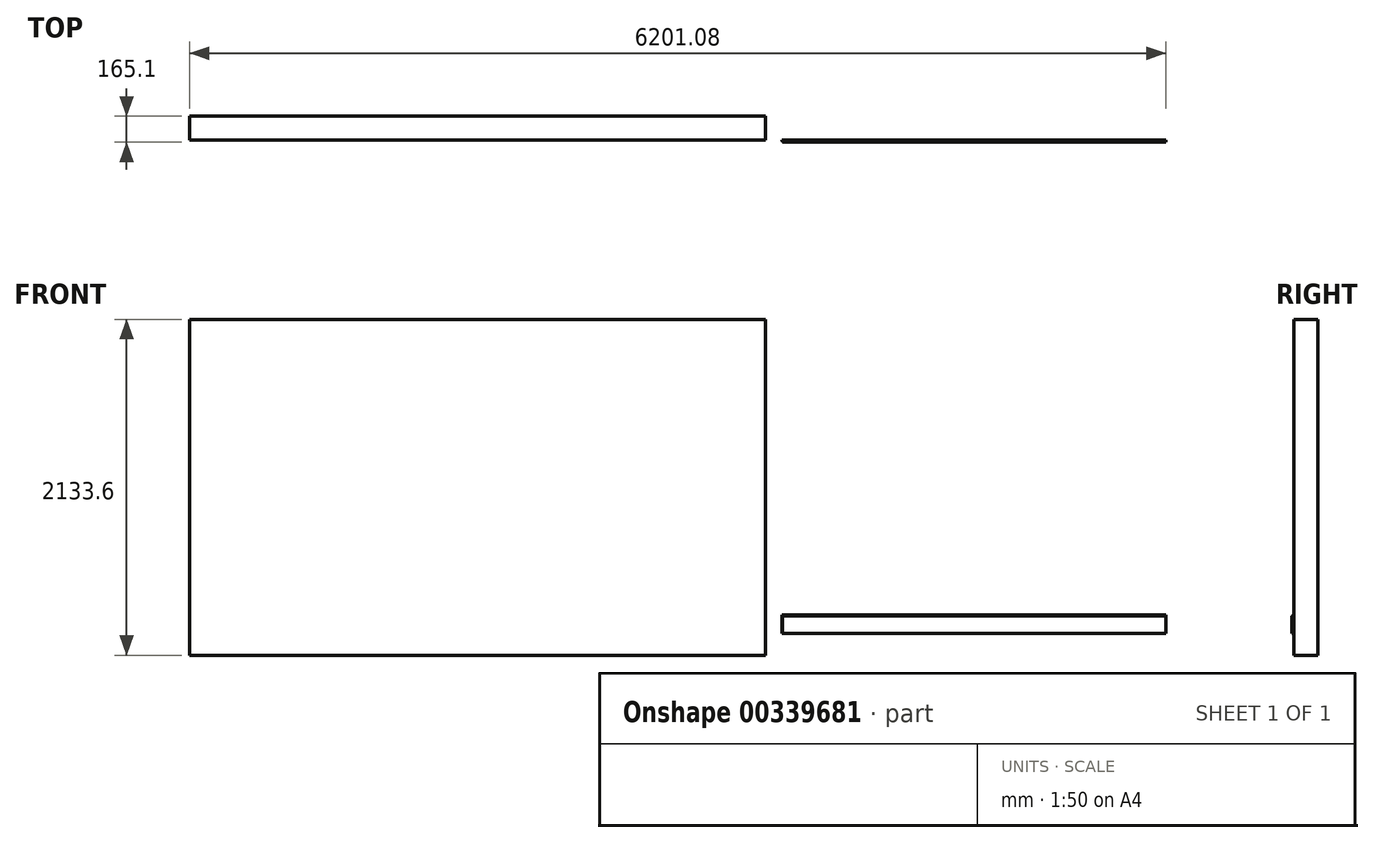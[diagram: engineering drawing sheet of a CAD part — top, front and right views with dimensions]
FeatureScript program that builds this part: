
annotation { "Feature Type Name" : "Feature", "Feature Type Description" : "" }
export const myFeature = defineFeature(function(context is Context, id is Id, definition is map)
    precondition{}
    {
        {
            var Q0;
            Q0=qCreatedBy(makeId("Front.planeOp"),FACE);
            var sketch = newSketch(context, id + "F0", { "sketchPlane" : qUnion([Q0])});
            skLineSegment(sketch, "E0.bottom", {"start": v(-3602.13, 2084.47) * mm, "end": v(55.47, 2084.47) * mm});
            skLineSegment(sketch, "E0.top", {"start": v(-3602.13, -49.13) * mm, "end": v(55.47, -49.13) * mm});
            skLineSegment(sketch, "E0.left", {"start": v(-3602.13, 2084.47) * mm, "end": v(-3602.13, -49.13) * mm});
            skLineSegment(sketch, "E0.right", {"start": v(55.47, 2084.47) * mm, "end": v(55.47, -49.13) * mm});
            skLineSegment(sketch, "E1.top", {"start": v(-3602.13, 90.57) * mm, "end": v(55.47, 90.57) * mm});
            skLineSegment(sketch, "E1.left", {"start": v(-3602.13, -49.13) * mm, "end": v(-3602.13, 90.57) * mm});
            skLineSegment(sketch, "E1.right", {"start": v(55.47, -49.13) * mm, "end": v(55.47, 90.57) * mm});
            skLineSegment(sketch, "E2.bottom", {"start": v(-736.02, 90.57) * mm, "end": v(160.55, 90.57) * mm});
            skLineSegment(sketch, "E2.top", {"start": v(-736.02, 208.05) * mm, "end": v(160.55, 208.05) * mm});
            skLineSegment(sketch, "E2.left", {"start": v(160.55, 90.57) * mm, "end": v(160.55, 208.05) * mm});
            skLineSegment(sketch, "E2.right", {"start": v(-736.02, 90.57) * mm, "end": v(-736.02, 208.05) * mm});
            skLineSegment(sketch, "E3.bottom", {"start": v(-2014.63, 208.05) * mm, "end": v(423.77, 208.05) * mm});
            skLineSegment(sketch, "E3.top", {"start": v(-2014.63, 325.52) * mm, "end": v(423.77, 325.52) * mm});
            skLineSegment(sketch, "E3.left", {"start": v(-2014.63, 208.05) * mm, "end": v(-2014.63, 325.52) * mm});
            skLineSegment(sketch, "E3.right", {"start": v(423.77, 208.05) * mm, "end": v(423.77, 325.52) * mm});
            skLineSegment(sketch, "E4.bottom", {"start": v(-2481.5, 325.52) * mm, "end": v(-43.1, 325.52) * mm});
            skLineSegment(sketch, "E4.top", {"start": v(-2481.5, 443) * mm, "end": v(-43.1, 443) * mm});
            skLineSegment(sketch, "E4.left", {"start": v(-2481.5, 325.52) * mm, "end": v(-2481.5, 443) * mm});
            skLineSegment(sketch, "E4.right", {"start": v(-43.1, 325.52) * mm, "end": v(-43.1, 443) * mm});
            skLineSegment(sketch, "E5.bottom", {"start": v(-794.93, 443) * mm, "end": v(-3233.33, 443) * mm});
            skLineSegment(sketch, "E5.top", {"start": v(-794.93, 560.47) * mm, "end": v(-3233.33, 560.47) * mm});
            skLineSegment(sketch, "E5.left", {"start": v(-794.93, 443) * mm, "end": v(-794.93, 560.47) * mm});
            skLineSegment(sketch, "E5.right", {"start": v(-3233.33, 443) * mm, "end": v(-3233.33, 560.47) * mm});
            skLineSegment(sketch, "E6.bottom", {"start": v(-1497.86, 560.47) * mm, "end": v(940.54, 560.47) * mm});
            skLineSegment(sketch, "E6.top", {"start": v(-1497.86, 677.95) * mm, "end": v(940.54, 677.95) * mm});
            skLineSegment(sketch, "E6.left", {"start": v(-1497.86, 560.47) * mm, "end": v(-1497.86, 677.95) * mm});
            skLineSegment(sketch, "E6.right", {"start": v(940.54, 560.47) * mm, "end": v(940.54, 677.95) * mm});
            skLineSegment(sketch, "E7.bottom", {"start": v(160.55, 208.05) * mm, "end": v(2598.95, 208.05) * mm});
            skLineSegment(sketch, "E7.top", {"start": v(162.08, 201.7) * mm, "end": v(2597.43, 201.7) * mm});
            skLineSegment(sketch, "E7.left", {"start": v(160.55, 208.05) * mm, "end": v(160.55, 201.7) * mm});
            skLineSegment(sketch, "E7.right", {"start": v(2598.95, 208.05) * mm, "end": v(2598.95, 201.7) * mm});
            skLineSegment(sketch, "E8.bottom", {"start": v(160.55, 208.05) * mm, "end": v(162.08, 208.05) * mm});
            skLineSegment(sketch, "E8.top", {"start": v(160.55, 90.57) * mm, "end": v(162.08, 90.57) * mm});
            skLineSegment(sketch, "E8.left", {"start": v(160.55, 208.05) * mm, "end": v(160.55, 90.57) * mm});
            skLineSegment(sketch, "E8.right", {"start": v(162.08, 201.7) * mm, "end": v(162.08, 90.57) * mm});
            skLineSegment(sketch, "E9.top", {"start": v(2598.95, 90.57) * mm, "end": v(2597.43, 90.57) * mm});
            skLineSegment(sketch, "E9.left", {"start": v(2598.95, 201.7) * mm, "end": v(2598.95, 90.57) * mm});
            skLineSegment(sketch, "E9.right", {"start": v(2597.43, 201.7) * mm, "end": v(2597.43, 90.57) * mm});
            skLineSegment(sketch, "E10", {"start": v(162.08, 90.57) * mm, "end": v(2598.95, 90.57) * mm});
            skSolve(sketch);
        }
        {
            var Q0;
            Q0=makeQuery(id+"F0.imprint","IMPRINT",FACE,{"disambiguationData":[TD([[makeQuery(id+"F0.imprint","IMPRINT",EDGE,{"derivedFrom":sQuery(id+"F0.wireOp",EDGE,"E7.top")}),-1.0]])]});
            extrude(context, id + "F1", {"entities" : qUnion([Q0]), "depth" : 12.7 * mm, "offsetDistance" : 25.4 * mm});
        }
        {
            var Q0;
            Q0=makeQuery(id+"F0.imprint","IMPRINT",FACE,{"disambiguationData":[TD([[makeQuery(id+"F0.imprint","IMPRINT",EDGE,{"derivedFrom":sQuery(id+"F0.wireOp",EDGE,"E7.top")}),1.0]])]});
            extrude(context, id + "F2", {"entities" : qUnion([Q0]), "operationType" : NewBodyOperationType.ADD, "depth" : 6.35 * mm, "offsetDistance" : 25.4 * mm});
        }
        {
            var Q0;
            {var subQ7=sQuery(id+"F0.wireOp",EDGE,"E0.bottom");Q0=makeQuery(id+"F0.imprint","IMPRINT",FACE,{"disambiguationData":[TD([[makeQuery(id+"F0.imprint","IMPRINT",EDGE,{"derivedFrom":subQ7}),-1.0]])]});}
            var Q1;
            {var subQ0=sQuery(id+"F0.wireOp",EDGE,"E6.left");Q1=makeQuery(id+"F0.imprint","IMPRINT",FACE,{"disambiguationData":[TD([[makeQuery(id+"F0.imprint","IMPRINT",EDGE,{"derivedFrom":subQ0}),-1.0]])]});}
            var Q2;
            Q2=makeQuery(id+"F0.imprint","IMPRINT",FACE,{"disambiguationData":[TD([[makeQuery(id+"F0.imprint","IMPRINT",EDGE,{"derivedFrom":sQuery(id+"F0.wireOp",EDGE,"E4.top")}),1.0]])]});
            var Q3;
            {var subQ1=sQuery(id+"F0.wireOp",EDGE,"E5.top");Q3=makeQuery(id+"F0.imprint","IMPRINT",FACE,{"disambiguationData":[TD([[makeQuery(id+"F0.imprint","IMPRINT",EDGE,{"derivedFrom":subQ1}),1.0]])]});}
            var Q4;
            {var subQ1=sQuery(id+"F0.wireOp",EDGE,"E4.top");Q4=makeQuery(id+"F0.imprint","IMPRINT",FACE,{"disambiguationData":[TD([[makeQuery(id+"F0.imprint","IMPRINT",EDGE,{"derivedFrom":subQ1}),-1.0]])]});}
            var Q5;
            {var subQ7=sQuery(id+"F0.wireOp",EDGE,"E3.left");Q5=makeQuery(id+"F0.imprint","IMPRINT",FACE,{"disambiguationData":[TD([[makeQuery(id+"F0.imprint","IMPRINT",EDGE,{"derivedFrom":subQ7}),-1.0]])]});}
            var Q6;
            {var subQ5=sQuery(id+"F0.wireOp",EDGE,"E2.right");Q6=makeQuery(id+"F0.imprint","IMPRINT",FACE,{"disambiguationData":[TD([[makeQuery(id+"F0.imprint","IMPRINT",EDGE,{"derivedFrom":subQ5}),-1.0]])]});}
            var Q7;
            Q7=makeQuery(id+"F0.imprint","IMPRINT",FACE,{"disambiguationData":[TD([[makeQuery(id+"F0.imprint","IMPRINT",EDGE,{"derivedFrom":sQuery(id+"F0.wireOp",EDGE,"E0.top")}),1.0]])]});
            extrude(context, id + "F3", {"entities" : qUnion([Q0, Q1, Q2, Q3, Q4, Q5, Q6, Q7]), "oppositeDirection" : true, "depth" : 152.4 * mm, "offsetDistance" : 25.4 * mm});
        }
    });
